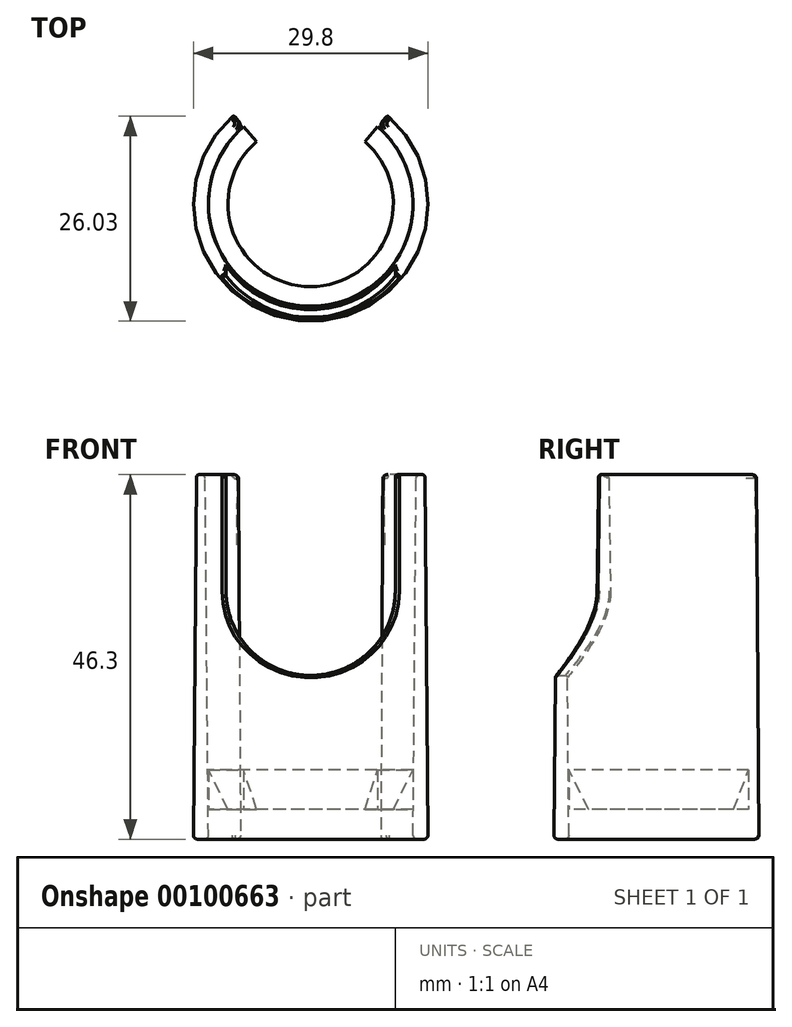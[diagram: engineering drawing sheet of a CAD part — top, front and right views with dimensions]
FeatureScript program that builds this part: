
annotation { "Feature Type Name" : "Feature", "Feature Type Description" : "" }
export const myFeature = defineFeature(function(context is Context, id is Id, definition is map)
    precondition{}
    {
        {
            var Q0;
            Q0=qCreatedBy(makeId("Top.planeOp"),FACE);
            var sketch = newSketch(context, id + "F0", { "sketchPlane" : qUnion([Q0])});
            skCircle(sketch, "E0", {"center": v(0, 0) * mm, "radius": 14.9 * mm});
            skCircle(sketch, "E1", {"center": v(0, 0) * mm, "radius": 13 * mm});
            skSolve(sketch);
        }
        {
            var Q0;
            Q0=qSketchRegion(id+"F0",true);
            extrude(context, id + "F1", {"entities" : qUnion([Q0]), "depth" : 46.3 * mm, "hasDraft" : true, "draftAngle" : .5 * degree, "draftPullDirection" : true});
        }
        {
            var Q0;
            Q0=makeQuery(id+"F1.opExtrude","CAP_FACE",FACE,{"disambiguationData":[OSD([sQuery(id+"F0.wireOp",EDGE,"E0"),sQuery(id+"F0.wireOp",EDGE,"E1")])],"isStart":true});
            cPlane(context, id + "F2", {"entities" : qUnion([Q0]), "cplaneType" : CPlaneType.OFFSET, "offset" : 3.8 * mm, "oppositeDirection" : true, "width" : 150 * mm, "height" : 150 * mm});
        }
        {
            var Q0;
            Q0=qCreatedBy(id+"F2.planeOp",FACE);
            var sketch = newSketch(context, id + "F3", { "sketchPlane" : qUnion([Q0])});
            skCircle(sketch, "E2", {"center": v(0, 0) * mm, "radius": 13 * mm});
            skCircle(sketch, "E3", {"center": v(0, 0) * mm, "radius": 10.5 * mm});
            skSolve(sketch);
        }
        {
            var Q0;
            Q0 = qSketchRegion(id + "F3", true);
            extrude(context, id + "F4", {"entities" : qUnion([Q0]), "operationType" : NewBodyOperationType.ADD, "oppositeDirection" : true, "depth" : 5 * mm});
        }
        {
            var Q0;
            Q0=makeQuery(id+"F1.opExtrude","CAP_FACE",FACE,{"disambiguationData":[OSD([sQuery(id+"F0.wireOp",EDGE,"E0"),sQuery(id+"F0.wireOp",EDGE,"E1")])],"isStart":false});
            var sketch = newSketch(context, id + "F5", { "sketchPlane" : qUnion([Q0])});
            skArc(sketch, "E4", {"start": v(-9.76, 11.25) * mm, "mid": v(0, 14.9) * mm, "end": v(9.76, 11.25) * mm});
            skLineSegment(sketch, "E5", {"start": v(0, 0) * mm, "end": v(9.76, 11.25) * mm});
            skLineSegment(sketch, "E6", {"start": v(0, 0) * mm, "end": v(-9.76, 11.25) * mm});
            skSolve(sketch);
        }
        {
            var Q0;
            Q0=qSketchRegion(id+"F5",true);
            extrude(context, id + "F6", {"entities" : qUnion([Q0]), "operationType" : NewBodyOperationType.REMOVE, "endBound" : BoundingType.THROUGH_ALL, "oppositeDirection" : true, "depth" : 25 * mm});
        }
        {
            var Q0;
            Q0=makeQuery(id+"F1.opExtrude","CAP_FACE",FACE,{"disambiguationData":[OSD([sQuery(id+"F0.wireOp",EDGE,"E0"),sQuery(id+"F0.wireOp",EDGE,"E1")])],"isStart":false});
            var sketch = newSketch(context, id + "F7", { "sketchPlane" : qUnion([Q0])});
            skLineSegment(sketch, "E7.bottom", {"start": v(22.75, 18.4) * mm, "end": v(-22.55, 18.4) * mm});
            skLineSegment(sketch, "E7.top", {"start": v(22.75, 4) * mm, "end": v(-22.55, 4) * mm});
            skLineSegment(sketch, "E7.left", {"start": v(22.75, 18.4) * mm, "end": v(22.75, 4) * mm});
            skLineSegment(sketch, "E7.right", {"start": v(-22.55, 18.4) * mm, "end": v(-22.55, 4) * mm});
            skSolve(sketch);
        }
        {
            var Q0;
            Q0=makeQuery(id+"F1.opExtrude","CAP_FACE",FACE,{"disambiguationData":[OSD([sQuery(id+"F0.wireOp",EDGE,"E0"),sQuery(id+"F0.wireOp",EDGE,"E1")])],"isStart":true});
            var sketch = newSketch(context, id + "F8", { "sketchPlane" : qUnion([Q0])});
            skLineSegment(sketch, "E8.bottom", {"start": v(-15, -4) * mm, "end": v(15, -4) * mm});
            skLineSegment(sketch, "E8.top", {"start": v(-15, -14.5) * mm, "end": v(15, -14.5) * mm});
            skLineSegment(sketch, "E8.left", {"start": v(-15, -4) * mm, "end": v(-15, -14.5) * mm});
            skLineSegment(sketch, "E8.right", {"start": v(15, -4) * mm, "end": v(15, -14.5) * mm});
            skSolve(sketch);
        }
        {
            var Q0;
            Q0=makeQuery(id+"F6.boolean.opBoolean","COPY",EDGE,{"derivedFrom":makeQuery(id+"F6.opExtrude","SWEPT_EDGE",EDGE,{"disambiguationData":[OSD([sQuery(id+"F0.wireOp",EDGE,"E0"),sQuery(id+"F5.wireOp",EDGE,"EvXCyCfA-SfMF-DEea-wm4n-LuDUqPH1RyXM"),sQuery(id+"F5.wireOp",EDGE,"E4")])]})});
            var Q1;
            Q1=makeQuery(id+"F6.boolean.opBoolean","COPY",EDGE,{"derivedFrom":makeQuery(id+"F6.opExtrude","SWEPT_EDGE",EDGE,{"disambiguationData":[OSD([sQuery(id+"F0.wireOp",EDGE,"E0"),sQuery(id+"F5.wireOp",EDGE,"4ysp1RNV-DPTV-7z7o-yt4w-jkN3UbwDpxyN"),sQuery(id+"F5.wireOp",EDGE,"E4")])]})});
            var Q2;
            {var subQ0=makeQuery(id+"F1.opExtrude","SWEPT_FACE",FACE,{"disambiguationData":[OSD([sQuery(id+"F0.wireOp",EDGE,"E1")])]});Q2=qUnion([makeQuery(id+"F6.boolean.opBoolean","INTERSECT",EDGE,{"derivedFrom":[subQ0,makeQuery(id+"F6.opExtrude","SWEPT_FACE",FACE,{"disambiguationData":[OSD([sQuery(id+"F5.wireOp",EDGE,"E5")])]})]}),makeQuery(id+"F6.boolean.opBoolean","INTERSECT",EDGE,{"derivedFrom":[subQ0,makeQuery(id+"F6.opExtrude","SWEPT_FACE",FACE,{"disambiguationData":[OSD([sQuery(id+"F5.wireOp",EDGE,"E6")])]})]})]);}
            var Q3;
            {var subQ0=makeQuery(id+"F1.opExtrude","SWEPT_FACE",FACE,{"disambiguationData":[OSD([sQuery(id+"F0.wireOp",EDGE,"E1")])]});Q3=qUnion([makeQuery(id+"F6.boolean.opBoolean","INTERSECT",EDGE,{"derivedFrom":[subQ0,makeQuery(id+"F6.opExtrude","SWEPT_FACE",FACE,{"disambiguationData":[OSD([sQuery(id+"F5.wireOp",EDGE,"E5")])]})]}),makeQuery(id+"F6.boolean.opBoolean","INTERSECT",EDGE,{"derivedFrom":[subQ0,makeQuery(id+"F6.opExtrude","SWEPT_FACE",FACE,{"disambiguationData":[OSD([sQuery(id+"F5.wireOp",EDGE,"E6")])]})]})]);}
            fillet(context, id + "F9", {"entities" : qUnion([Q0, Q1, Q2, Q3]), "radius" : 1 * mm, "tangentPropagation" : true, "allowEdgeOverflow" : false});
        }
        {
            var Q0;
            Q0=qCreatedBy(makeId("Front.planeOp"),FACE);
            var sketch = newSketch(context, id + "F10", { "sketchPlane" : qUnion([Q0])});
            skArc(sketch, "E9", {"start": v(-10.75, 31.55) * mm, "mid": v(0, 20.8) * mm, "end": v(10.75, 31.55) * mm});
            skLineSegment(sketch, "E10", {"start": v(-10.75, 31.55) * mm, "end": v(-10.75, 47.13) * mm});
            skLineSegment(sketch, "E11", {"start": v(10.75, 31.55) * mm, "end": v(10.75, 47.13) * mm});
            skLineSegment(sketch, "E12", {"start": v(10.75, 47.13) * mm, "end": v(-10.75, 47.13) * mm});
            skSolve(sketch);
        }
        {
            var Q0;
            Q0=qSketchRegion(id+"F10",true);
            extrude(context, id + "F11", {"entities" : qUnion([Q0]), "operationType" : NewBodyOperationType.REMOVE, "depth" : 25 * mm});
        }
        {
            var Q0;
            Q0=makeQuery(id+"F11.boolean.opBoolean","INTERSECT",EDGE,{"derivedFrom":[makeQuery(id+"F1.opExtrude","SWEPT_FACE",FACE,{"disambiguationData":[OSD([sQuery(id+"F0.wireOp",EDGE,"E0")])]}),makeQuery(id+"F11.opExtrude","SWEPT_FACE",FACE,{"disambiguationData":[OSD([sQuery(id+"F10.wireOp",EDGE,"E9")])]})]});
            fillet(context, id + "F12", {"entities" : qUnion([Q0]), "radius" : .3 * mm, "tangentPropagation" : true, "allowEdgeOverflow" : false});
        }
        {
            var Q0;
            Q0=makeQuery(id+"F1.opExtrude","CAP_EDGE",EDGE,{"disambiguationData":[OSD([sQuery(id+"F0.wireOp",EDGE,"E0")])],"isStart":true});
            var Q1;
            Q1=makeQuery(id+"F1.opExtrude","CAP_EDGE",EDGE,{"disambiguationData":[OSD([sQuery(id+"F0.wireOp",EDGE,"E1")])],"isStart":true});
            var Q2;
            {var subQ0=sQuery(id+"F0.wireOp",EDGE,"E0");Q2=makeQuery(id+"F11.boolean.opBoolean","SPLIT",EDGE,{"disambiguationData":[TD([makeQuery(id+"F6.boolean.opBoolean","COPY",FACE,{"derivedFrom":makeQuery(id+"F6.opExtrude","SWEPT_FACE",FACE,{"disambiguationData":[OSD([sQuery(id+"F5.wireOp",EDGE,"4ysp1RNV-DPTV-7z7o-yt4w-jkN3UbwDpxyN")])]})})])],"derivedFrom":makeQuery(id+"F1.opExtrude","CAP_EDGE",EDGE,{"disambiguationData":[OSD([subQ0])],"isStart":false})});}
            var Q3;
            {var subQ0=sQuery(id+"F0.wireOp",EDGE,"E1");Q3=makeQuery(id+"F11.boolean.opBoolean","SPLIT",EDGE,{"disambiguationData":[TD([makeQuery(id+"F11.opExtrude","SWEPT_FACE",FACE,{"disambiguationData":[OSD([sQuery(id+"F10.wireOp",EDGE,"E11")])]})])],"derivedFrom":makeQuery(id+"F1.opExtrude","CAP_EDGE",EDGE,{"disambiguationData":[OSD([subQ0])],"isStart":false})});}
            var Q4;
            {var subQ0=sQuery(id+"F0.wireOp",EDGE,"E1");Q4=makeQuery(id+"F11.boolean.opBoolean","SPLIT",EDGE,{"disambiguationData":[TD([makeQuery(id+"F11.opExtrude","SWEPT_FACE",FACE,{"disambiguationData":[OSD([sQuery(id+"F10.wireOp",EDGE,"E10")])]})])],"derivedFrom":makeQuery(id+"F1.opExtrude","CAP_EDGE",EDGE,{"disambiguationData":[OSD([subQ0])],"isStart":false})});}
            var Q5;
            {var subQ0=sQuery(id+"F0.wireOp",EDGE,"E0");Q5=makeQuery(id+"F11.boolean.opBoolean","SPLIT",EDGE,{"disambiguationData":[TD([makeQuery(id+"F6.boolean.opBoolean","COPY",FACE,{"derivedFrom":makeQuery(id+"F6.opExtrude","SWEPT_FACE",FACE,{"disambiguationData":[OSD([sQuery(id+"F5.wireOp",EDGE,"EvXCyCfA-SfMF-DEea-wm4n-LuDUqPH1RyXM")])]})})])],"derivedFrom":makeQuery(id+"F1.opExtrude","CAP_EDGE",EDGE,{"disambiguationData":[OSD([subQ0])],"isStart":false})});}
            fillet(context, id + "F13", {"entities" : qUnion([Q0, Q1, Q2, Q3, Q4, Q5]), "radius" : .5 * mm, "tangentPropagation" : true, "allowEdgeOverflow" : false});
        }
        {
            var Q0;
            Q0=makeQuery(id+"F6.boolean.opBoolean","INTERSECT",EDGE,{"derivedFrom":[makeQuery(id+"F1.opExtrude","SWEPT_FACE",FACE,{"disambiguationData":[OSD([sQuery(id+"F0.wireOp",EDGE,"E0")])]}),makeQuery(id+"F6.opExtrude","SWEPT_FACE",FACE,{"disambiguationData":[OSD([sQuery(id+"F5.wireOp",EDGE,"E6")])]})]});
            fillet(context, id + "F14", {"entities" : qUnion([Q0]), "radius" : .28 * mm, "tangentPropagation" : true, "allowEdgeOverflow" : false});
        }
        {
            var Q0;
            Q0=makeQuery(id+"F4.opExtrude","CAP_EDGE",EDGE,{"disambiguationData":[OSD([sQuery(id+"F3.wireOp",EDGE,"E3")])],"isStart":false});
            chamfer(context, id + "F15", {"entities" : qUnion([Q0]), "chamferType" : ChamferType.TWO_OFFSETS, "width1" : 2.5 * mm, "oppositeDirection" : false, "width2" : 5 * mm, "tangentPropagation" : true});
        }
    });
